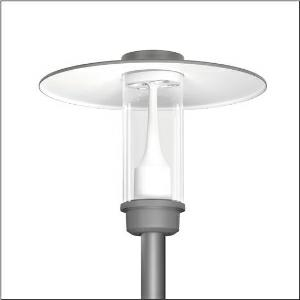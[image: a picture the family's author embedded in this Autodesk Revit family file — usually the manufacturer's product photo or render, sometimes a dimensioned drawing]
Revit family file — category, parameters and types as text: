
# Revit family: litepole_2_iq___st1_2a_5xa5425af14hp_29a9
name_source: partatom
category: Lighting Fixtures
units: mm (PartAtom-declared; Revit-internal decimal feet)

## family parameters
Cut with Voids When Loaded = No
Host = Face
Light Source = No
Part Type = Normal
Room Calculation Point = No
Round Connector Dimension = Use Diameter
Shared = No

## types (1)
- --- (1 x LED, 3940 lm, 33.6 W, 2200K)
    Apparent Load = 34 VA
    CIE Flux Codes = 22 59 92 98 100
    Color Rendering = 70
    Color Temperature = 2200K
    Default Elevation = 1800 mm
    Description = Litepole 2 iQ, mast luminaire, Module 540 iQ-SR, primary light control with 3 zone facetted reflector, of plastic, silver coated, highly specular, structured, primary optical cover: cover, of PMMA, transparent, light distribution: ST1.2a, light emission: direct distribution, primary light characteristic: asymmetric, installation type: post-top, LED, High Power LED, rated luminous flux: 3.940lm, luminous efficacy: 117lm/W, light colour: 722, colour temperature: 2200K, control gear: iQ Street-Remote, control: pre-setting: logarithmic dimming characteristic, Street-Remote, Auto-Match, Temp-Guard, Lumen-Switch, Night-Set, Smart-Wire, Light-Fading, Desk-Remote (wireless, voltage-free reading and setting of iQ features in the workshop via application-optimized NFC function/RFID function), optimised constant luminous flux control (CLO 2.0), with terminal, 6-pole, max. 2.5mm², mains connection: 230..240V, AC, 50/60Hz, start of lifetime: 34W, end of service life: 36W, reduction: 15W, luminaire housing, upper part, of aluminium, coated, Siteco® metallic grey (DB 702S), diameter: 750mm, height: 590mm, spigot size: d x l = 76 x 70mm (post-top) | with reducer (optional accessory) 60 x 70mm, mounting height: 3..5m, post-top mast mounting element, of diecast aluminium, coated, Siteco® metallic grey (DB 702S), Module 540 iQ-SR, traffic white (RAL 9016), equipment: Power, protection rating (complete): IP65, insulation class (complete): insulation class II (safety insulation), certification: CE, ENEC, VDE, packaging unit: 1 piece

Light Distribution: ST1.2a
    Height = 590 mm
    Lamp = 1 x LED
    Lamp Light Flux = 3940 lm
    Lamp Power = 33.6 W
    Lamp count = 1
    Length = 750 mm
    Luminous efficacy = 117 lm/W
    Manufacturer = Siteco
    ModVariant = No
    Model = 5XA5425AF14HP
    Number of Poles = 1
    OnlyDefault = Yes
    Power Factor = 1
    Product Name = Litepole 2 iQ | ST1.2a
    Product group = mast luminaire | pylon top
    ProductGroupID = 6100
    Protection Class = Protection class II
    Protection Degree = IP 65
    RLX_Detail_Level = 1
    RLX_Emergency_Light_Flux = 0 lm
    RLX_Emergency_Type = 0
    RLX_Emergency_Type_DB = No
    RlxData = <blob elided: 31937 chars, md5=8e3bb90e>
    Socket = socket
    Standby Power = 0 W
    System Light Flux = 3940 lm
    System Power = 34 W
    Type Comments = factory setting: luminous flux: 100 % | dim-lin: 254 | 695 mA
    Type Image = l_1006518.jpg
    URL = http://relux.com
    VarID = @adj_189761
    Voltage = 0 V
    Weight = 0.00 kg
    Width = 0 mm  [stored 0 ft]

note: [stored X ft] marks values corroborated as IEEE doubles in the binary element streams (Revit-internal decimal feet)

## geometry (parser evidence)
native form markers: Blend x4, Sweep x11
no freeform markers — native parametric forms only
